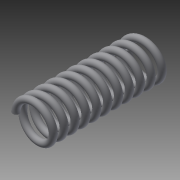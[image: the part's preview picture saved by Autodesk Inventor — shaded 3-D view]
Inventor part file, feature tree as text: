
AUTODESK INVENTOR PART (.ipt)
format: ipt  version: 2013 (Build 170138000, 138)  size: 776,192 bytes
history: native  units: mm
features: helix x1, sketch x1
ambient origin geometry x8: Origin, YZ Plane, XZ Plane, XY Plane, X Axis, Y Axis, Z Axis, Center Point
bodies: Solid1 (feature_tree)
feature tree (2):
  helix  "Coil1"  [1 undecoded]
  sketch  "Sketch1"  dims[d2=2.3749mm d3=10.0mm d4=12.5mm d5=100.0mm d6=0.0mm d7=90.0deg d8=90.0deg d9=90.0deg d10=90.0deg]
note: 1 required parameter value undecoded (feature->parameter linkage not recoverable at this tier; creation-order binding heuristic only, values carry confidence <= 0.55)
